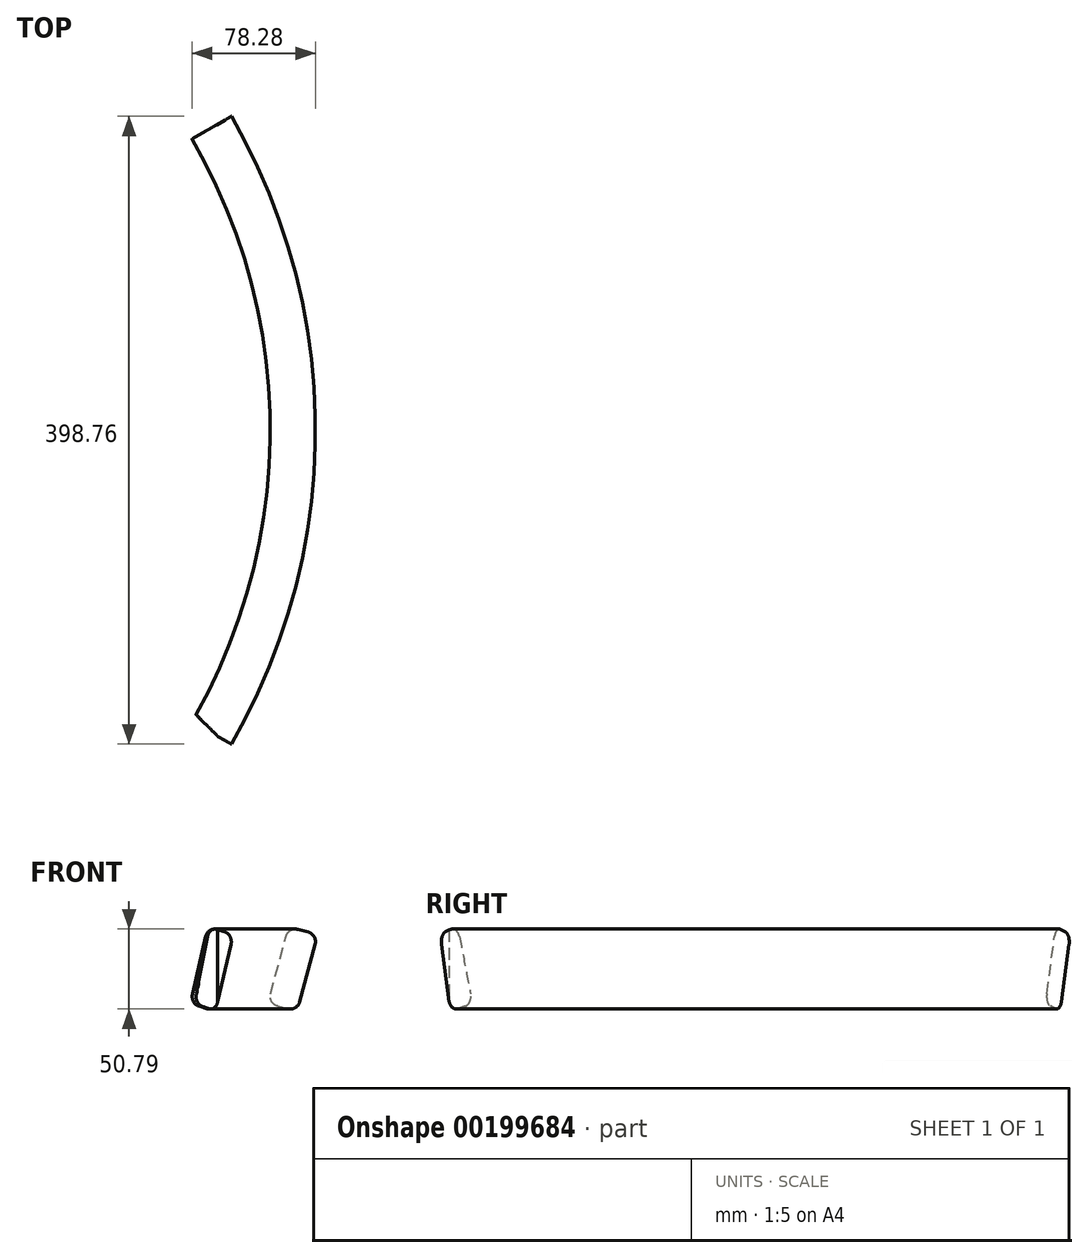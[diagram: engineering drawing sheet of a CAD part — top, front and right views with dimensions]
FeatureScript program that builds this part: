
annotation { "Feature Type Name" : "Feature", "Feature Type Description" : "" }
export const myFeature = defineFeature(function(context is Context, id is Id, definition is map)
    precondition{}
    {
        {
            var Q0;
            Q0=qCreatedBy(makeId("Front.planeOp"),FACE);
            var sketch = newSketch(context, id + "F0", { "sketchPlane" : qUnion([Q0])});
            skLineSegment(sketch, "E0", {"start": v(1.64, 6.13) * mm, "end": v(11.4, 42.56) * mm});
            skLineSegment(sketch, "E1", {"start": v(19.18, 47.05) * mm, "end": v(25.42, 45.38) * mm});
            skLineSegment(sketch, "E2", {"start": v(29.91, 37.6) * mm, "end": v(20.15, 1.17) * mm});
            skLineSegment(sketch, "E3", {"start": v(12.38, -3.32) * mm, "end": v(6.13, -1.64) * mm});
            skLineSegment(sketch, "E4", {"start": v(0, 0) * mm, "end": v(0, 61.12) * mm, "construction": true});
            skPoint(sketch, "E5.visualSharp", {"position": v(13.05, 48.7) * mm});
            skArc(sketch, "E5.filletArc", {"start": v(19.18, 47.05) * mm, "mid": v(14.36, 46.41) * mm, "end": v(11.4, 42.56) * mm});
            skPoint(sketch, "E6.visualSharp", {"position": v(31.56, 43.73) * mm});
            skArc(sketch, "E6.filletArc", {"start": v(29.91, 37.6) * mm, "mid": v(29.28, 42.42) * mm, "end": v(25.42, 45.38) * mm});
            skPoint(sketch, "E7.visualSharp", {"position": v(18.51, -4.96) * mm});
            skArc(sketch, "E7.filletArc", {"start": v(12.38, -3.32) * mm, "mid": v(17.2, -2.68) * mm, "end": v(20.15, 1.17) * mm});
            skPoint(sketch, "E8.visualSharp", {"position": v(0, 0) * mm});
            skArc(sketch, "E8.filletArc", {"start": v(1.64, 6.13) * mm, "mid": v(2.28, 1.32) * mm, "end": v(6.13, -1.64) * mm});
            skSolve(sketch);
        }
        {
            var Q0;
            Q0=qCreatedBy(makeId("Top.planeOp"),FACE);
            var sketch = newSketch(context, id + "F1", { "sketchPlane" : qUnion([Q0])});
            skLineSegment(sketch, "E9", {"start": v(460.5, 0) * mm, "end": v(-540.2, 0) * mm, "construction": true});
            skCircle(sketch, "E10", {"center": v(-368.62, 0) * mm, "radius": 381 * mm});
            skSolve(sketch);
        }
        {
            var Q0;
            Q0=makeQuery(id+"F0.imprint","IMPRINT",FACE,{"disambiguationData":[TD([[makeQuery(id+"F0.imprint","IMPRINT",EDGE,{"derivedFrom":sQuery(id+"F0.wireOp",EDGE,"E0")}),-1.0]])]});
            var Q1;
            Q1=sQuery(id+"F1.wireOp",EDGE,"E10");
            revolve(context, id + "F2", {"entities" : qUnion([Q0]), "axis" : qUnion([Q1]), "revolveType" : RevolveType.TWO_DIRECTIONS, "angle" : 30 * degree, "angleBack" : 330 * degree});
        }
        {
            var Q0;
            Q0=makeQuery(id+"F1.imprint","IMPRINT",FACE,{"disambiguationData":[TD([[makeQuery(id+"F1.imprint","IMPRINT",EDGE,{"derivedFrom":sQuery(id+"F1.wireOp",EDGE,"E10")}),1.0]])]});
            cPlane(context, id + "F3", {"entities" : qUnion([Q0]), "cplaneType" : CPlaneType.OFFSET, "offset" : 6.35 * mm, "oppositeDirection" : true, "width" : 152.4 * mm, "height" : 152.4 * mm});
        }
        {
            var Q0;
            Q0=qCreatedBy(id+"F3.planeOp",FACE);
            var sketch = newSketch(context, id + "F4", { "sketchPlane" : qUnion([Q0])});
            skLineSegment(sketch, "E11", {"start": v(-22.1, -204.21) * mm, "end": v(-57.87, -168.45) * mm});
            skLineSegment(sketch, "E12", {"start": v(-57.87, -168.45) * mm, "end": v(-66.02, -178.86) * mm});
            skLineSegment(sketch, "E13", {"start": v(-66.02, -178.86) * mm, "end": v(-22.1, -204.21) * mm});
            skSolve(sketch);
        }
        {
            var Q0;
            Q0=makeQuery(id+"F4.imprint","IMPRINT",FACE,{"disambiguationData":[TD([[makeQuery(id+"F4.imprint","IMPRINT",EDGE,{"derivedFrom":sQuery(id+"F4.wireOp",EDGE,"E11")}),1.0]])]});
            extrude(context, id + "F5", {"entities" : qUnion([Q0]), "operationType" : NewBodyOperationType.REMOVE, "depth" : 76.2 * mm});
        }
    });
